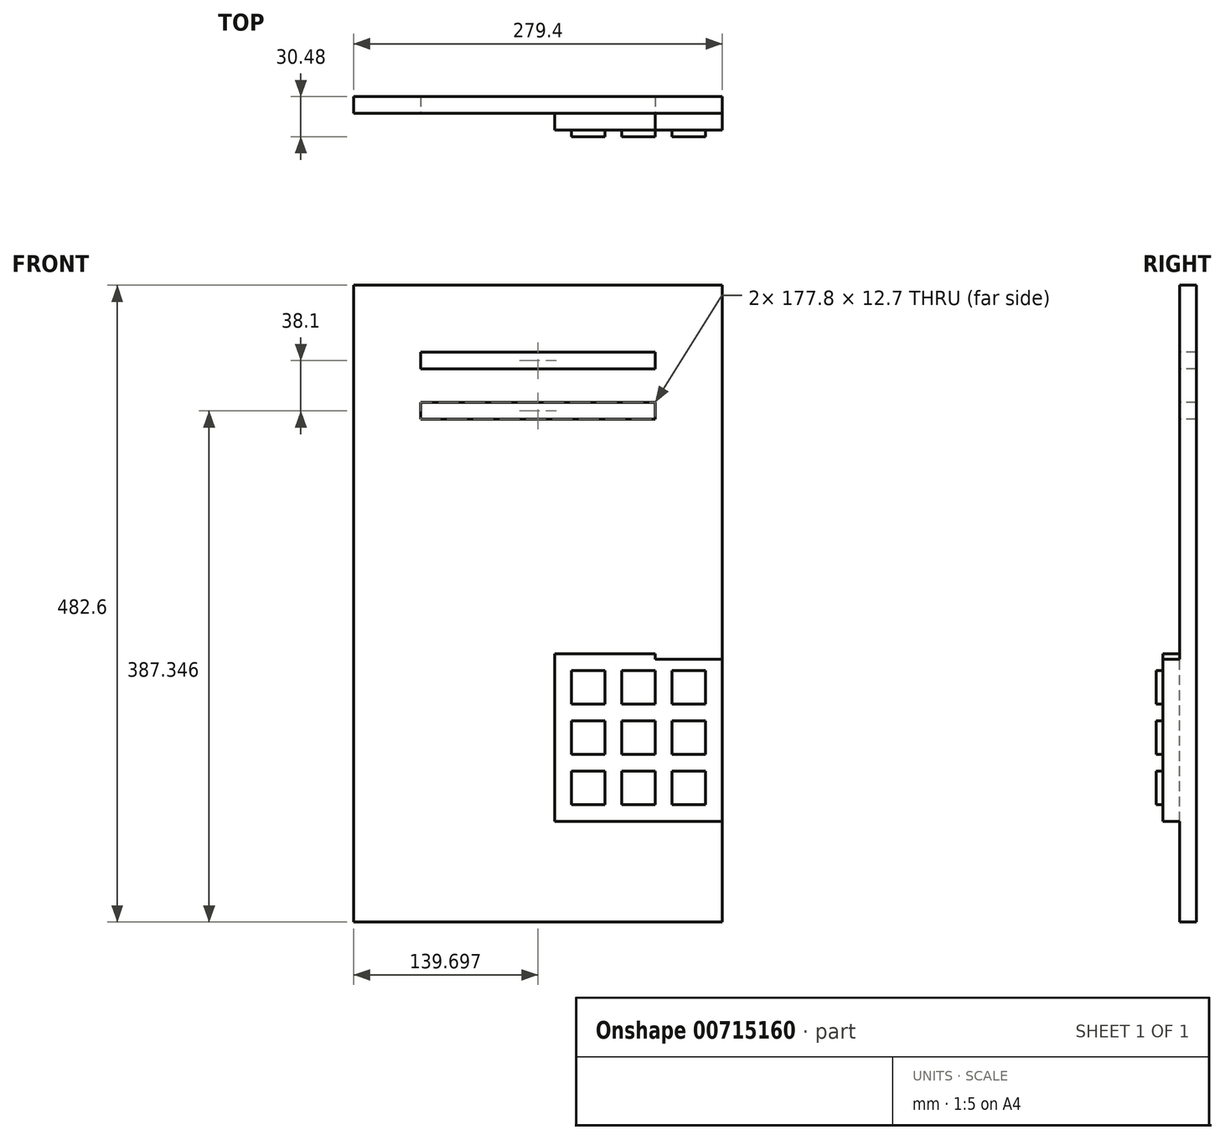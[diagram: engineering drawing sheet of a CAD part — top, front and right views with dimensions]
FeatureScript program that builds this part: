
annotation { "Feature Type Name" : "Feature", "Feature Type Description" : "" }
export const myFeature = defineFeature(function(context is Context, id is Id, definition is map)
    precondition{}
    {
        {
            var Q0;
            Q0=qCreatedBy(makeId("Front.planeOp"),FACE);
            var sketch = newSketch(context, id + "F0", { "sketchPlane" : qUnion([Q0])});
            skLineSegment(sketch, "E0.bottom", {"start": v(-137.06, 213.95) * mm, "end": v(142.34, 213.95) * mm});
            skLineSegment(sketch, "E0.top", {"start": v(-137.06, -268.65) * mm, "end": v(142.34, -268.65) * mm});
            skLineSegment(sketch, "E0.left", {"start": v(-137.06, 213.95) * mm, "end": v(-137.06, -268.65) * mm});
            skLineSegment(sketch, "E0.right", {"start": v(142.34, 213.95) * mm, "end": v(142.34, -268.65) * mm});
            skSolve(sketch);
        }
        {
            var Q0;
            Q0=makeQuery(id+"F0.imprint","IMPRINT",FACE,{"disambiguationData":[TD([[makeQuery(id+"F0.imprint","IMPRINT",EDGE,{"derivedFrom":sQuery(id+"F0.wireOp",EDGE,"E0.bottom")}),-1.0]])]});
            extrude(context, id + "F1", {"entities" : qUnion([Q0]), "depth" : 12.7 * mm, "offsetDistance" : 25.4 * mm});
        }
        {
            var Q0;
            Q0=makeQuery(id+"F1.opExtrude","CAP_FACE",FACE,{"disambiguationData":[OSD([sQuery(id+"F0.wireOp",EDGE,"E0.bottom"),sQuery(id+"F0.wireOp",EDGE,"E0.top"),sQuery(id+"F0.wireOp",EDGE,"E0.left"),sQuery(id+"F0.wireOp",EDGE,"E0.right")])],"isStart":false});
            var sketch = newSketch(context, id + "F2", { "sketchPlane" : qUnion([Q0])});
            skLineSegment(sketch, "E1.bottom", {"start": v(-86.26, 163.15) * mm, "end": v(91.54, 163.15) * mm});
            skLineSegment(sketch, "E1.top", {"start": v(-86.26, 150.45) * mm, "end": v(91.54, 150.45) * mm});
            skLineSegment(sketch, "E1.left", {"start": v(-86.26, 163.15) * mm, "end": v(-86.26, 150.45) * mm});
            skLineSegment(sketch, "E1.right", {"start": v(91.54, 163.15) * mm, "end": v(91.54, 150.45) * mm});
            skLineSegment(sketch, "E2.bottom", {"start": v(-86.26, 125.05) * mm, "end": v(91.54, 125.05) * mm});
            skLineSegment(sketch, "E2.top", {"start": v(-86.26, 112.35) * mm, "end": v(91.54, 112.35) * mm});
            skLineSegment(sketch, "E2.left", {"start": v(-86.26, 125.05) * mm, "end": v(-86.26, 112.35) * mm});
            skLineSegment(sketch, "E2.right", {"start": v(91.54, 125.05) * mm, "end": v(91.54, 112.35) * mm});
            skLineSegment(sketch, "E3.bottom", {"start": v(142.34, -69.49) * mm, "end": v(91.54, -69.49) * mm});
            skLineSegment(sketch, "E3.top", {"start": v(142.34, -44.09) * mm, "end": v(91.54, -44.09) * mm});
            skLineSegment(sketch, "E3.left", {"start": v(142.34, -69.49) * mm, "end": v(142.34, -44.09) * mm});
            skLineSegment(sketch, "E3.right", {"start": v(91.54, -69.49) * mm, "end": v(91.54, -44.09) * mm});
            skSolve(sketch);
        }
        {
            var Q0;
            Q0=makeQuery(id+"F2.imprint","IMPRINT",FACE,{"disambiguationData":[TD([[makeQuery(id+"F2.imprint","IMPRINT",EDGE,{"derivedFrom":sQuery(id+"F2.wireOp",EDGE,"E1.bottom")}),-1.0]])]});
            var Q1;
            Q1=makeQuery(id+"F2.imprint","IMPRINT",FACE,{"disambiguationData":[TD([[makeQuery(id+"F2.imprint","IMPRINT",EDGE,{"derivedFrom":sQuery(id+"F2.wireOp",EDGE,"E2.bottom")}),-1.0]])]});
            extrude(context, id + "F3", {"entities" : qUnion([Q0, Q1]), "operationType" : NewBodyOperationType.REMOVE, "oppositeDirection" : true, "depth" : 25.4 * mm, "offsetDistance" : 25.4 * mm});
        }
        {
            var Q0;
            Q0=makeQuery(id+"F2.imprint","IMPRINT",FACE,{"disambiguationData":[TD([[makeQuery(id+"F2.imprint","IMPRINT",EDGE,{"derivedFrom":sQuery(id+"F2.wireOp",EDGE,"E3.bottom")}),-1.0]])]});
            extrude(context, id + "F4", {"entities" : qUnion([Q0]), "operationType" : NewBodyOperationType.REMOVE, "oppositeDirection" : true, "depth" : 25.4 * mm, "offsetDistance" : 25.4 * mm});
        }
        {
            var Q0;
            Q0=makeQuery(id+"F4.boolean.opBoolean","COPY",FACE,{"derivedFrom":makeQuery(id+"F4.opExtrude","SWEPT_FACE",FACE,{"disambiguationData":[OSD([sQuery(id+"F2.wireOp",EDGE,"E3.right")])]})});
            var sketch = newSketch(context, id + "F5", { "sketchPlane" : qUnion([Q0])});
            skLineSegment(sketch, "E4.bottom", {"start": v(-12.7, -44.09) * mm, "end": v(0, -44.09) * mm});
            skLineSegment(sketch, "E4.top", {"start": v(-12.7, -69.49) * mm, "end": v(0, -69.49) * mm});
            skLineSegment(sketch, "E4.left", {"start": v(-12.7, -44.09) * mm, "end": v(-12.7, -69.49) * mm});
            skLineSegment(sketch, "E4.right", {"start": v(0, -44.09) * mm, "end": v(0, -69.49) * mm});
            skSolve(sketch);
        }
        {
            var Q0;
            Q0=makeQuery(id+"F5.imprint","IMPRINT",FACE,{"disambiguationData":[TD([[makeQuery(id+"F5.imprint","IMPRINT",EDGE,{"derivedFrom":sQuery(id+"F5.wireOp",EDGE,"E4.bottom")}),1.0]])]});
            extrude(context, id + "F6", {"entities" : qUnion([Q0]), "operationType" : NewBodyOperationType.ADD, "depth" : 50.8 * mm, "offsetDistance" : 25.4 * mm});
        }
        {
            var Q0;
            Q0=makeQuery(id+"F2.imprint","IMPRINT",FACE,{"disambiguationData":[TD([[makeQuery(id+"F2.imprint","IMPRINT",EDGE,{"derivedFrom":sQuery(id+"F2.wireOp",EDGE,"E1.bottom")}),1.0]])]});
            var sketch = newSketch(context, id + "F7", { "sketchPlane" : qUnion([Q0])});
            skLineSegment(sketch, "E5.bottom", {"start": v(142.34, -192.45) * mm, "end": v(15.34, -192.45) * mm});
            skLineSegment(sketch, "E5.top", {"start": v(142.34, -65.45) * mm, "end": v(15.34, -65.45) * mm});
            skLineSegment(sketch, "E5.left", {"start": v(142.34, -192.45) * mm, "end": v(142.34, -65.45) * mm});
            skLineSegment(sketch, "E5.right", {"start": v(15.34, -192.45) * mm, "end": v(15.34, -65.45) * mm});
            skLineSegment(sketch, "E6.bottom", {"start": v(28.04, -78.15) * mm, "end": v(53.44, -78.15) * mm});
            skLineSegment(sketch, "E6.top", {"start": v(28.04, -103.55) * mm, "end": v(53.44, -103.55) * mm});
            skLineSegment(sketch, "E6.left", {"start": v(28.04, -78.15) * mm, "end": v(28.04, -103.55) * mm});
            skLineSegment(sketch, "E6.right", {"start": v(53.44, -78.15) * mm, "end": v(53.44, -103.55) * mm});
            skLineSegment(sketch, "E7.bottom", {"start": v(66.14, -78.15) * mm, "end": v(91.54, -78.15) * mm});
            skLineSegment(sketch, "E7.top", {"start": v(66.14, -103.55) * mm, "end": v(91.54, -103.55) * mm});
            skLineSegment(sketch, "E7.left", {"start": v(66.14, -78.15) * mm, "end": v(66.14, -103.55) * mm});
            skLineSegment(sketch, "E7.right", {"start": v(91.54, -78.15) * mm, "end": v(91.54, -103.55) * mm});
            skLineSegment(sketch, "E8.bottom", {"start": v(104.24, -78.15) * mm, "end": v(129.64, -78.15) * mm});
            skLineSegment(sketch, "E8.top", {"start": v(104.24, -103.55) * mm, "end": v(129.64, -103.55) * mm});
            skLineSegment(sketch, "E8.left", {"start": v(104.24, -78.15) * mm, "end": v(104.24, -103.55) * mm});
            skLineSegment(sketch, "E8.right", {"start": v(129.64, -78.15) * mm, "end": v(129.64, -103.55) * mm});
            skLineSegment(sketch, "E9.bottom", {"start": v(28.04, -116.25) * mm, "end": v(53.44, -116.25) * mm});
            skLineSegment(sketch, "E9.top", {"start": v(28.04, -141.65) * mm, "end": v(53.44, -141.65) * mm});
            skLineSegment(sketch, "E9.left", {"start": v(28.04, -116.25) * mm, "end": v(28.04, -141.65) * mm});
            skLineSegment(sketch, "E9.right", {"start": v(53.44, -116.25) * mm, "end": v(53.44, -141.65) * mm});
            skLineSegment(sketch, "E10.bottom", {"start": v(66.14, -116.25) * mm, "end": v(91.54, -116.25) * mm});
            skLineSegment(sketch, "E10.top", {"start": v(66.14, -141.65) * mm, "end": v(91.54, -141.65) * mm});
            skLineSegment(sketch, "E10.left", {"start": v(66.14, -116.25) * mm, "end": v(66.14, -141.65) * mm});
            skLineSegment(sketch, "E10.right", {"start": v(91.54, -116.25) * mm, "end": v(91.54, -141.65) * mm});
            skLineSegment(sketch, "E11.bottom", {"start": v(104.24, -116.25) * mm, "end": v(129.64, -116.25) * mm});
            skLineSegment(sketch, "E11.top", {"start": v(104.24, -141.65) * mm, "end": v(129.64, -141.65) * mm});
            skLineSegment(sketch, "E11.left", {"start": v(104.24, -116.25) * mm, "end": v(104.24, -141.65) * mm});
            skLineSegment(sketch, "E11.right", {"start": v(129.64, -116.25) * mm, "end": v(129.64, -141.65) * mm});
            skLineSegment(sketch, "E12.bottom", {"start": v(28.04, -154.35) * mm, "end": v(53.44, -154.35) * mm});
            skLineSegment(sketch, "E12.top", {"start": v(28.04, -179.75) * mm, "end": v(53.44, -179.75) * mm});
            skLineSegment(sketch, "E12.left", {"start": v(28.04, -154.35) * mm, "end": v(28.04, -179.75) * mm});
            skLineSegment(sketch, "E12.right", {"start": v(53.44, -154.35) * mm, "end": v(53.44, -179.75) * mm});
            skLineSegment(sketch, "E13.bottom", {"start": v(66.14, -154.35) * mm, "end": v(91.54, -154.35) * mm});
            skLineSegment(sketch, "E13.top", {"start": v(66.14, -179.75) * mm, "end": v(91.54, -179.75) * mm});
            skLineSegment(sketch, "E13.left", {"start": v(66.14, -154.35) * mm, "end": v(66.14, -179.75) * mm});
            skLineSegment(sketch, "E13.right", {"start": v(91.54, -154.35) * mm, "end": v(91.54, -179.75) * mm});
            skLineSegment(sketch, "E14.bottom", {"start": v(104.24, -154.35) * mm, "end": v(129.64, -154.35) * mm});
            skLineSegment(sketch, "E14.top", {"start": v(104.24, -179.75) * mm, "end": v(129.64, -179.75) * mm});
            skLineSegment(sketch, "E14.left", {"start": v(104.24, -154.35) * mm, "end": v(104.24, -179.75) * mm});
            skLineSegment(sketch, "E14.right", {"start": v(129.64, -154.35) * mm, "end": v(129.64, -179.75) * mm});
            skSolve(sketch);
        }
        {
            var Q0;
            Q0=makeQuery(id+"F7.imprint","IMPRINT",FACE,{"disambiguationData":[TD([[makeQuery(id+"F7.imprint","IMPRINT",EDGE,{"derivedFrom":sQuery(id+"F7.wireOp",EDGE,"E6.bottom")}),-1.0]])]});
            var Q1;
            Q1=makeQuery(id+"F7.imprint","IMPRINT",FACE,{"disambiguationData":[TD([[makeQuery(id+"F7.imprint","IMPRINT",EDGE,{"derivedFrom":sQuery(id+"F7.wireOp",EDGE,"E7.bottom")}),-1.0]])]});
            var Q2;
            Q2=makeQuery(id+"F7.imprint","IMPRINT",FACE,{"disambiguationData":[TD([[makeQuery(id+"F7.imprint","IMPRINT",EDGE,{"derivedFrom":sQuery(id+"F7.wireOp",EDGE,"E8.bottom")}),-1.0]])]});
            var Q3;
            Q3=makeQuery(id+"F7.imprint","IMPRINT",FACE,{"disambiguationData":[TD([[makeQuery(id+"F7.imprint","IMPRINT",EDGE,{"derivedFrom":sQuery(id+"F7.wireOp",EDGE,"E14.bottom")}),-1.0]])]});
            var Q4;
            Q4=makeQuery(id+"F7.imprint","IMPRINT",FACE,{"disambiguationData":[TD([[makeQuery(id+"F7.imprint","IMPRINT",EDGE,{"derivedFrom":sQuery(id+"F7.wireOp",EDGE,"E13.bottom")}),-1.0]])]});
            var Q5;
            Q5=makeQuery(id+"F7.imprint","IMPRINT",FACE,{"disambiguationData":[TD([[makeQuery(id+"F7.imprint","IMPRINT",EDGE,{"derivedFrom":sQuery(id+"F7.wireOp",EDGE,"E12.bottom")}),-1.0]])]});
            var Q6;
            Q6=makeQuery(id+"F7.imprint","IMPRINT",FACE,{"disambiguationData":[TD([[makeQuery(id+"F7.imprint","IMPRINT",EDGE,{"derivedFrom":sQuery(id+"F7.wireOp",EDGE,"E9.bottom")}),-1.0]])]});
            var Q7;
            Q7=makeQuery(id+"F7.imprint","IMPRINT",FACE,{"disambiguationData":[TD([[makeQuery(id+"F7.imprint","IMPRINT",EDGE,{"derivedFrom":sQuery(id+"F7.wireOp",EDGE,"E10.bottom")}),-1.0]])]});
            var Q8;
            Q8=makeQuery(id+"F7.imprint","IMPRINT",FACE,{"disambiguationData":[TD([[makeQuery(id+"F7.imprint","IMPRINT",EDGE,{"derivedFrom":sQuery(id+"F7.wireOp",EDGE,"E11.bottom")}),-1.0]])]});
            extrude(context, id + "F8", {"entities" : qUnion([Q0, Q1, Q2, Q3, Q4, Q5, Q6, Q7, Q8]), "operationType" : NewBodyOperationType.ADD, "depth" : 17.78 * mm, "offsetDistance" : 25.4 * mm});
        }
        {
            var Q0;
            {var subQ3=sQuery(id+"F7.wireOp",EDGE,"E5.bottom");Q0=makeQuery(id+"F7.imprint","IMPRINT",FACE,{"disambiguationData":[TD([[makeQuery(id+"F7.imprint","IMPRINT",EDGE,{"derivedFrom":subQ3}),-1.0]])]});}
            extrude(context, id + "F9", {"entities" : qUnion([Q0]), "operationType" : NewBodyOperationType.ADD, "depth" : 12.7 * mm, "offsetDistance" : 25.4 * mm});
        }
    });
